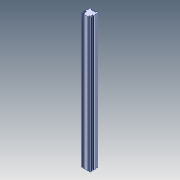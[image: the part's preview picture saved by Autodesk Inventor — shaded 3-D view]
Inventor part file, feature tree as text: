
AUTODESK INVENTOR PART (.ipt)
format: ipt  version: 2020 (Build 240168000, 168)  size: 379,904 bytes
history: native  units: mm
features: other x4, projected_geometry x3, extrude x2, sketch x2
ambient origin geometry x8: Origin, YZ Plane, XZ Plane, XY Plane, X Axis, Y Axis, Z Axis, Center Point
bodies: Body1 (feature_tree), Body2 (feature_tree)
feature tree (11):
  other  "ソリッド1"
  extrude  "押し出し1"  Depth=600.0mm TaperAngle=0.0deg
  extrude  "押し出し2"  Depth=672.0mm TaperAngle=0.0deg
  other  "ソリッド2"
  sketch  "スケッチ1"
  projected_geometry  "投影ループ1"
  projected_geometry  "投影ループ2"
  sketch  "スケッチ2"
  projected_geometry  "投影ループ3"
  other  "Boss-Extrude1[1]"
  other  "Boss-Extrude1[2]"
